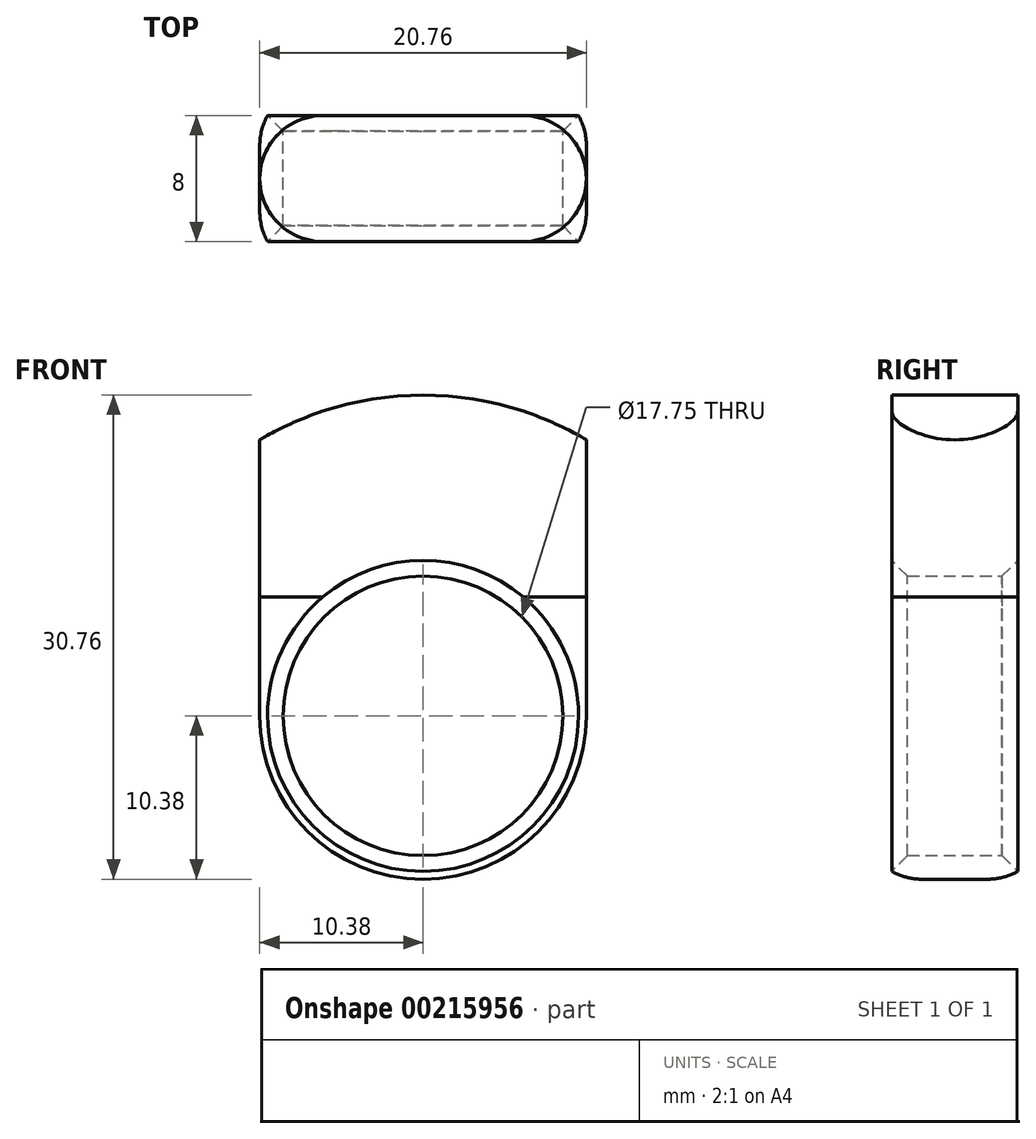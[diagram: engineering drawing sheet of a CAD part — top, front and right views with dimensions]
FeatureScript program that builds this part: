
annotation { "Feature Type Name" : "Feature", "Feature Type Description" : "" }
export const myFeature = defineFeature(function(context is Context, id is Id, definition is map)
    precondition{}
    {
        {
            var Q0;
            Q0=qCreatedBy(makeId("Front.planeOp"),FACE);
            var sketch = newSketch(context, id + "F0", { "sketchPlane" : qUnion([Q0])});
            skCircle(sketch, "E0", {"center": v(0, 0) * mm, "radius": 8.88 * mm});
            skCircle(sketch, "E1.0", {"center": v(0, 0) * mm, "radius": 10.38 * mm});
            skCircle(sketch, "E2.0", {"center": v(0, 0) * mm, "radius": 20.38 * mm});
            skLineSegment(sketch, "E3", {"start": v(10.38, 0) * mm, "end": v(10.38, 17.54) * mm});
            skLineSegment(sketch, "E4.MirrorCS", {"start": v(-10.38, 0) * mm, "end": v(-10.38, 17.54) * mm});
            skCircle(sketch, "E5.0", {"center": v(0, 0) * mm, "radius": 19.38 * mm});
            skLineSegment(sketch, "E6", {"start": v(-0.5, 20.37) * mm, "end": v(-0.5, 19.37) * mm});
            skLineSegment(sketch, "E7.MirrorCS", {"start": v(0.5, 20.37) * mm, "end": v(0.5, 19.37) * mm});
            skLineSegment(sketch, "E8", {"start": v(0, 20.38) * mm, "end": v(0, 19.38) * mm});
            skLineSegment(sketch, "E9", {"start": v(-5.56, 19.6) * mm, "end": v(-5.56, 18.56) * mm});
            skSolve(sketch);
        }
        {
            var Q0;
            Q0=makeQuery(id+"F0.imprint","IMPRINT",FACE,{"disambiguationData":[TD([[makeQuery(id+"F0.imprint","IMPRINT",EDGE,{"derivedFrom":sQuery(id+"F0.wireOp",EDGE,"E0")}),-1.0]])]});
            extrude(context, id + "F1", {"entities" : qUnion([Q0]), "depth" : 4 * mm, "hasSecondDirection" : true, "secondDirectionOppositeDirection" : true, "secondDirectionDepth" : 4 * mm});
        }
        {
            var Q0;
            Q0=makeQuery(id+"F1.opExtrude","CAP_EDGE",EDGE,{"disambiguationData":[OSD([sQuery(id+"F0.wireOp",EDGE,"E0")])],"isStart":false});
            var Q1;
            Q1=makeQuery(id+"F1.opExtrude","CAP_EDGE",EDGE,{"disambiguationData":[OSD([sQuery(id+"F0.wireOp",EDGE,"E0")])],"isStart":true});
            chamfer(context, id + "F2", {"entities" : qUnion([Q0, Q1]), "width" : 1 * mm, "tangentPropagation" : true});
        }
        {
            var Q0;
            {var subQ0=sQuery(id+"F0.wireOp",EDGE,"E3");var subQ1=sQuery(id+"F0.wireOp",EDGE,"E1.0");var subQ2=makeQuery(id+"F0.imprint","INTERSECT",VERTEX,{"derivedFrom":[subQ1,subQ0]});Q0=makeQuery(id+"F0.imprint","IMPRINT",FACE,{"disambiguationData":[TD([[makeQuery(id+"F0.imprint","IMPRINT",EDGE,{"disambiguationData":[TD([[subQ2,-1.0]])],"derivedFrom":subQ1}),-1.0]])]});}
            var Q1;
            {var subQ0=sQuery(id+"F0.wireOp",EDGE,"E3");var subQ1=sQuery(id+"F0.wireOp",EDGE,"E2.0");var subQ2=makeQuery(id+"F0.imprint","INTERSECT",VERTEX,{"derivedFrom":[subQ1,subQ0]});Q1=makeQuery(id+"F0.imprint","IMPRINT",FACE,{"disambiguationData":[TD([[makeQuery(id+"F0.imprint","IMPRINT",EDGE,{"disambiguationData":[TD([[subQ2,-1.0]])],"derivedFrom":subQ1}),1.0]])]});}
            var Q2;
            {var subQ0=sQuery(id+"F0.wireOp",EDGE,"E7.MirrorCS");Q2=makeQuery(id+"F0.imprint","IMPRINT",FACE,{"disambiguationData":[TD([[makeQuery(id+"F0.imprint","IMPRINT",EDGE,{"derivedFrom":subQ0}),-1.0]])]});}
            var Q3;
            {var subQ3=sQuery(id+"F0.wireOp",EDGE,"E9");Q3=makeQuery(id+"F0.imprint","IMPRINT",FACE,{"disambiguationData":[TD([[makeQuery(id+"F0.imprint","IMPRINT",EDGE,{"derivedFrom":subQ3}),-1.0]])]});}
            var Q4;
            {var subQ0=sQuery(id+"F0.wireOp",EDGE,"E6");Q4=makeQuery(id+"F0.imprint","IMPRINT",FACE,{"disambiguationData":[TD([[makeQuery(id+"F0.imprint","IMPRINT",EDGE,{"derivedFrom":subQ0}),-1.0]])]});}
            var Q5;
            {var subQ0=sQuery(id+"F0.wireOp",EDGE,"E6");Q5=makeQuery(id+"F0.imprint","IMPRINT",FACE,{"disambiguationData":[TD([[makeQuery(id+"F0.imprint","IMPRINT",EDGE,{"derivedFrom":subQ0}),1.0]])]});}
            extrude(context, id + "F3", {"entities" : qUnion([Q0, Q1, Q2, Q3, Q4, Q5]), "operationType" : NewBodyOperationType.ADD, "depth" : 4 * mm, "hasSecondDirection" : true, "secondDirectionOppositeDirection" : true, "secondDirectionDepth" : 4 * mm});
        }
        {
            var Q0;
            Q0=makeQuery(id+"F3.opExtrude","CAP_EDGE",EDGE,{"disambiguationData":[OSD([sQuery(id+"F0.wireOp",EDGE,"E3")])],"isStart":false});
            var Q1;
            Q1=makeQuery(id+"F3.opExtrude","CAP_EDGE",EDGE,{"disambiguationData":[OSD([sQuery(id+"F0.wireOp",EDGE,"E3")])],"isStart":true});
            var Q2;
            Q2=makeQuery(id+"F3.opExtrude","CAP_EDGE",EDGE,{"disambiguationData":[OSD([sQuery(id+"F0.wireOp",EDGE,"E4.MirrorCS")])],"isStart":false});
            var Q3;
            Q3=makeQuery(id+"F3.opExtrude","CAP_EDGE",EDGE,{"disambiguationData":[OSD([sQuery(id+"F0.wireOp",EDGE,"E4.MirrorCS")])],"isStart":true});
            fillet(context, id + "F4", {"entities" : qUnion([Q0, Q1, Q2, Q3]), "radius" : 4 * mm, "tangentPropagation" : true, "allowEdgeOverflow" : false});
        }
    });
